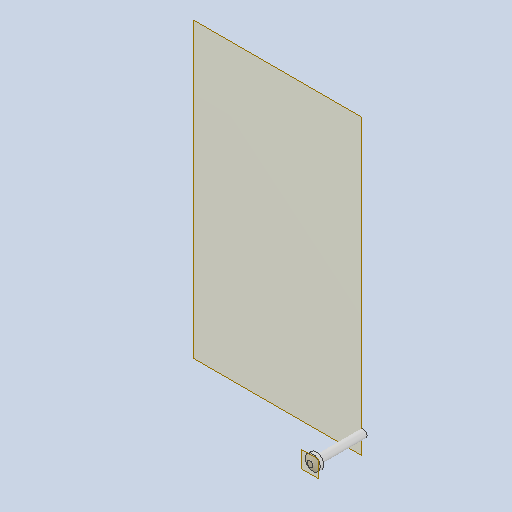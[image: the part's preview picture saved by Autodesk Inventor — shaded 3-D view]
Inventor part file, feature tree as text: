
AUTODESK INVENTOR PART (.ipt)
format: ipt  version: 2023 (Build 270158000, 158)  size: 154,112 bytes
history: native  units: mm
features: other x5, sketch x3, plane x2, extrude x2, loft x1, reference x1, projected_geometry x1
ambient origin geometry x8: Origin, YZ Plane, XZ Plane, XY Plane, X Axis, Y Axis, Z Axis, Center Point
bodies: Solid1 (feature_tree)
feature tree (15):
  plane  "Work Plane1"
  extrude  "Extrusion1"  Depth=17.9mm TaperAngle=0.0deg
  extrude  "Extrusion2"  Depth=1.35mm TaperAngle=0.0deg
  plane  "Work Plane2"
  loft  "Loft1"
  sketch  "Sketch1"  dims[d1=2.9mm d2=17.9mm d3=0.0mm]
  reference  "Reference1"
  sketch  "Sketch2"  dims[d4=5.83mm d5=1.35mm d6=0.0mm]
  projected_geometry  "Projected Loop1"
  sketch  "Sketch3"  dims[d7=1.01mm d8=0.0mm d9=90.0deg d10=0.0mm d11=90.0deg]
  other  "Edges1"
  parser-record x1  (decoder bookkeeping rows leaked as tree rows — omitted from the tree; the rows remain in map.json)
  other  "doorLockAssembly_V4.iam"
  other  "housingFront:1"
  other  "housingPlate:1"
note: 1 file-system path scrubbed to <path> (originals preserved in map.json)
